# Revit family: Heater-Bromic-Eclipse-Electric-Wall-Mounted_EU_2
name_source: partatom
category: Mechanical Equipment
units: mm (PartAtom-declared; Revit-internal decimal feet)

## family parameters
Classification = None
Cut with Voids When Loaded = No
Host = Face
OmniClass Number = 23.75.10.14
OmniClass Title = Independent Electric Heating Units
Part Type = Normal
Room Calculation Point = No
Round Connector Dimension = Use Diameter
Shared = No

## types (1)
- Eclipse Electric - Wall Mounted
    Apparent Load = 3000 VA
    Approximate Heat Area = 11.00 m²
    Default Elevation = 2198 mm  [stored 7.21129 ft]
    Depth = 1549 mm
    Description = The Eclipse Smart-Heat Electric heater is equipped with 3 different heat outputs up to 2900W and a dimmable LED light railing. Available in six unique mounting options, the Eclipse Smart-Heat™ series adds style, warmth and light to design-focused outdoor spaces.
    Diameter = 711 mm
    FloorClearance = 2438 mm
    Frequency = 60 Hz
    Height = 559 mm
    Load Classification = Other
    Load Sub-Classification Motor = No
    Manufacturer = Bromic Heating
    Material = Metal-Steel-Bromic-Black
    Model = Eclipse Smart-Heat™ Electric
    Mounting Type Info = Wall Mounted
    Number of Poles = 1
    Power Factor = 1
    Product data url = https://www.bimobject.com
    ProductCode = BH0920011
    SideClearance = 457 mm
    URL = https://www.bromic.co.uk
    Utility = No
    Voltage = 240 V
    Wattage = 3000 W
    calcClearanceFront = 807 mm
    calcClearanceWidth = 1614 mm

note: [stored X ft] marks values corroborated as IEEE doubles in the binary element streams (Revit-internal decimal feet)

## geometry (parser evidence)
native form markers: Sweep x2
no freeform markers — native parametric forms only
